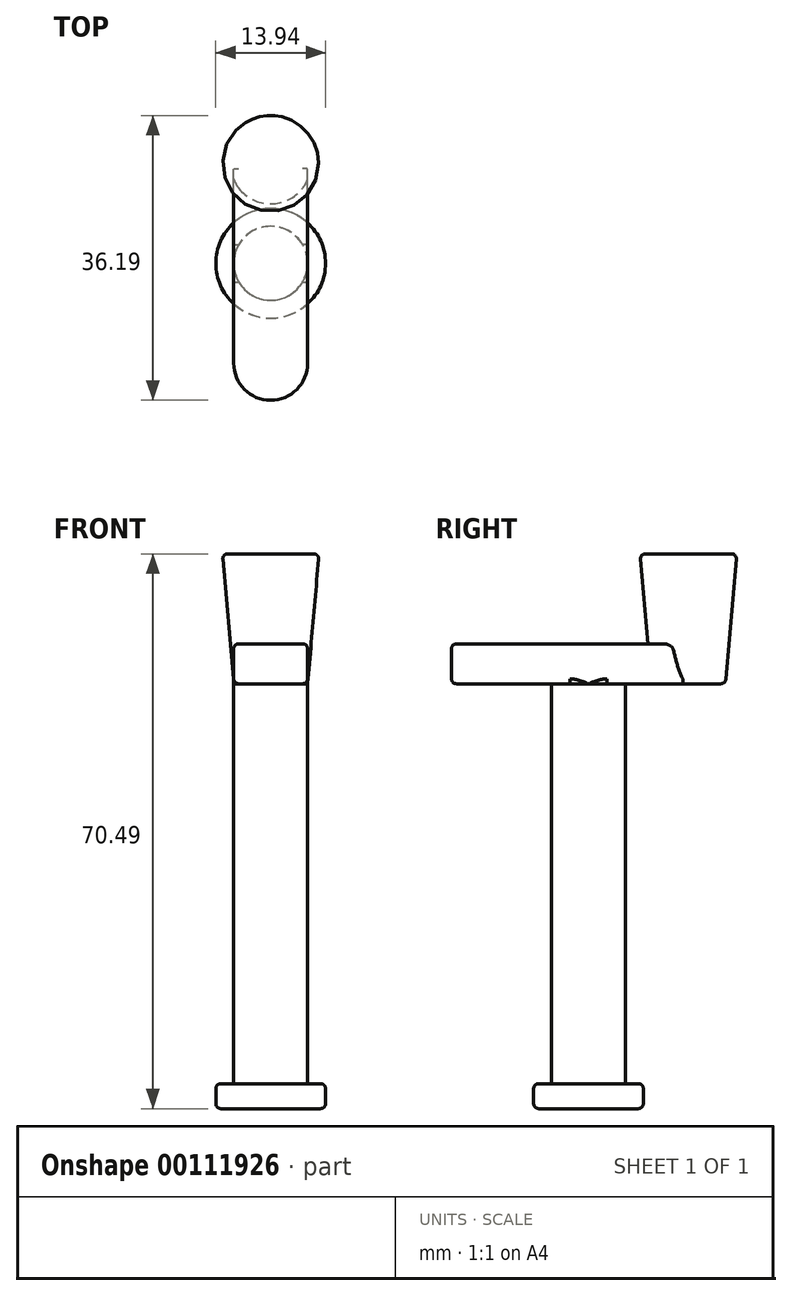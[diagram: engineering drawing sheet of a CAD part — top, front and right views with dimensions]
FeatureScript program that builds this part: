
annotation { "Feature Type Name" : "Feature", "Feature Type Description" : "" }
export const myFeature = defineFeature(function(context is Context, id is Id, definition is map)
    precondition{}
    {
        {
            var Q0;
            Q0=qCreatedBy(makeId("Top.planeOp"),FACE);
            var sketch = newSketch(context, id + "F0", { "sketchPlane" : qUnion([Q0])});
            skLineSegment(sketch, "E0.bottom", {"start": v(4.7, -12.7) * mm, "end": v(-4.7, -12.7) * mm});
            skLineSegment(sketch, "E0.top", {"start": v(4.7, 12.7) * mm, "end": v(-4.7, 12.7) * mm});
            skLineSegment(sketch, "E0.left", {"start": v(4.7, -12.7) * mm, "end": v(4.7, 12.7) * mm});
            skLineSegment(sketch, "E0.right", {"start": v(-4.7, -12.7) * mm, "end": v(-4.7, 12.7) * mm});
            skPoint(sketch, "E0.middle", {"position": v(0, 0) * mm});
            skCircle(sketch, "E1", {"center": v(0, 12.7) * mm, "radius": 4.7 * mm});
            skCircle(sketch, "E2", {"center": v(0, -12.7) * mm, "radius": 4.7 * mm});
            skSolve(sketch);
        }
        {
            var Q0;
            {var subQ0=sQuery(id+"F0.wireOp",EDGE,"E0.left");Q0=makeQuery(id+"F0.imprint","IMPRINT",FACE,{"disambiguationData":[TD([[makeQuery(id+"F0.imprint","IMPRINT",EDGE,{"derivedFrom":subQ0}),1.0]])]});}
            var Q1;
            {var subQ0=sQuery(id+"F0.wireOp",EDGE,"E0.bottom");Q1=makeQuery(id+"F0.imprint","IMPRINT",FACE,{"disambiguationData":[TD([[makeQuery(id+"F0.imprint","IMPRINT",EDGE,{"derivedFrom":subQ0}),1.0]])]});}
            var Q2;
            {var subQ0=sQuery(id+"F0.wireOp",EDGE,"E0.bottom");Q2=makeQuery(id+"F0.imprint","IMPRINT",FACE,{"disambiguationData":[TD([[makeQuery(id+"F0.imprint","IMPRINT",EDGE,{"derivedFrom":subQ0}),-1.0]])]});}
            extrude(context, id + "F1", {"entities" : qUnion([Q0, Q1, Q2]), "depth" : 5.08 * mm});
        }
        {
            var Q0;
            {var subQ0=sQuery(id+"F0.wireOp",EDGE,"E0.top");Q0=makeQuery(id+"F0.imprint","IMPRINT",FACE,{"disambiguationData":[TD([[makeQuery(id+"F0.imprint","IMPRINT",EDGE,{"derivedFrom":subQ0}),1.0]])]});}
            var Q1;
            {var subQ0=sQuery(id+"F0.wireOp",EDGE,"E0.top");Q1=makeQuery(id+"F0.imprint","IMPRINT",FACE,{"disambiguationData":[TD([[makeQuery(id+"F0.imprint","IMPRINT",EDGE,{"derivedFrom":subQ0}),-1.0]])]});}
            extrude(context, id + "F2", {"entities" : qUnion([Q0, Q1]), "operationType" : NewBodyOperationType.ADD, "depth" : 16.5 * mm, "hasDraft" : true, "draftAngle" : 5 * degree});
        }
        {
            var Q0;
            {var subQ0=sQuery(id+"F0.wireOp",EDGE,"E1");Q0=makeQuery(id+"F2.boolean.opBoolean","MERGE",FACE,{"derivedFrom":[makeQuery(id+"F1.opExtrude","CAP_FACE",FACE,{"disambiguationData":[OSD([sQuery(id+"F0.wireOp",EDGE,"E0.left"),sQuery(id+"F0.wireOp",EDGE,"E0.right"),subQ0,sQuery(id+"F0.wireOp",EDGE,"E2")])],"isStart":true}),makeQuery(id+"F2.opExtrude","CAP_FACE",FACE,{"disambiguationData":[OSD([subQ0])],"isStart":true})]});}
            var sketch = newSketch(context, id + "F3", { "sketchPlane" : qUnion([Q0])});
            skCircle(sketch, "E3", {"center": v(0, 0) * mm, "radius": 4.7 * mm});
            skSolve(sketch);
        }
        {
            var Q0;
            {var subQ0=sQuery(id+"F3.wireOp",EDGE,"E3");var subQ1=makeQuery(id+"F3.imprint","INTERSECT",VERTEX,{"derivedFrom":[makeQuery(id+"F1.opExtrude","CAP_EDGE",EDGE,{"disambiguationData":[OSD([sQuery(id+"F0.wireOp",EDGE,"E0.left")])],"isStart":true}),subQ0]});Q0=makeQuery(id+"F3.imprint","IMPRINT",FACE,{"disambiguationData":[TD([[makeQuery(id+"F3.imprint","IMPRINT",EDGE,{"disambiguationData":[TD([[subQ1,-1.0]])],"derivedFrom":subQ0}),1.0]])]});}
            extrude(context, id + "F4", {"entities" : qUnion([Q0]), "operationType" : NewBodyOperationType.ADD, "depth" : 50.8 * mm});
        }
        {
            var Q0;
            Q0=makeQuery(id+"F2.opExtrude","CAP_EDGE",EDGE,{"disambiguationData":[OSD([sQuery(id+"F0.wireOp",EDGE,"E1")])],"isStart":false});
            var Q1;
            Q1=makeQuery(id+"F1.opExtrude","CAP_EDGE",EDGE,{"disambiguationData":[OSD([sQuery(id+"F0.wireOp",EDGE,"E2")])],"isStart":false});
            var Q2;
            Q2=makeQuery(id+"F1.opExtrude","CAP_EDGE",EDGE,{"disambiguationData":[OSD([sQuery(id+"F0.wireOp",EDGE,"E2")])],"isStart":true});
            var Q3;
            {var subQ1=sQuery(id+"F0.wireOp",EDGE,"E0.right");var subQ2=sQuery(id+"F0.wireOp",EDGE,"E2");Q3=makeQuery(id+"F4.boolean.opBoolean","SPLIT",EDGE,{"disambiguationData":[TD([makeQuery(id+"F1.opExtrude","SWEPT_FACE",FACE,{"disambiguationData":[OSD([subQ2])]})])],"derivedFrom":makeQuery(id+"F1.opExtrude","CAP_EDGE",EDGE,{"disambiguationData":[OSD([subQ1])],"isStart":true})});}
            var Q4;
            {var subQ0=sQuery(id+"F0.wireOp",EDGE,"E1");var subQ1=sQuery(id+"F0.wireOp",EDGE,"E0.right");Q4=makeQuery(id+"F4.boolean.opBoolean","SPLIT",EDGE,{"disambiguationData":[TD([makeQuery(id+"F2.opExtrude","SWEPT_FACE",FACE,{"disambiguationData":[OSD([subQ0])]})])],"derivedFrom":makeQuery(id+"F1.opExtrude","CAP_EDGE",EDGE,{"disambiguationData":[OSD([subQ1])],"isStart":true})});}
            var Q5;
            Q5=makeQuery(id+"F2.opExtrude","CAP_EDGE",EDGE,{"disambiguationData":[OSD([sQuery(id+"F0.wireOp",EDGE,"E1")])],"isStart":true});
            var Q6;
            {var subQ0=sQuery(id+"F0.wireOp",EDGE,"E1");var subQ1=sQuery(id+"F0.wireOp",EDGE,"E0.left");Q6=makeQuery(id+"F4.boolean.opBoolean","SPLIT",EDGE,{"disambiguationData":[TD([makeQuery(id+"F2.opExtrude","SWEPT_FACE",FACE,{"disambiguationData":[OSD([subQ0])]})])],"derivedFrom":makeQuery(id+"F1.opExtrude","CAP_EDGE",EDGE,{"disambiguationData":[OSD([subQ1])],"isStart":true})});}
            var Q7;
            Q7=makeQuery(id+"F1.opExtrude","CAP_EDGE",EDGE,{"disambiguationData":[OSD([sQuery(id+"F0.wireOp",EDGE,"E0.left")])],"isStart":false});
            fillet(context, id + "F5", {"entities" : qUnion([Q0, Q1, Q2, Q3, Q4, Q5, Q6, Q7]), "radius" : 0.64 * mm, "tangentPropagation" : true, "allowEdgeOverflow" : false});
        }
        {
            var Q0;
            Q0=makeQuery(id+"F4.opExtrude","CAP_FACE",FACE,{"disambiguationData":[OSD([sQuery(id+"F3.wireOp",EDGE,"E3")])],"isStart":false});
            var sketch = newSketch(context, id + "F6", { "sketchPlane" : qUnion([Q0])});
            skCircle(sketch, "E4", {"center": v(0, 0) * mm, "radius": 6.97 * mm});
            skSolve(sketch);
        }
        {
            var Q0;
            Q0 = qSketchRegion(id + "F6", true);
            extrude(context, id + "F7", {"entities" : qUnion([Q0]), "operationType" : NewBodyOperationType.ADD, "depth" : 3.17 * mm});
        }
        {
            var Q0;
            Q0=makeQuery(id+"F4.opExtrude","CAP_EDGE",EDGE,{"disambiguationData":[OSD([sQuery(id+"F3.wireOp",EDGE,"E3")])],"isStart":false});
            var Q1;
            Q1=makeQuery(id+"F7.opExtrude","CAP_EDGE",EDGE,{"disambiguationData":[OSD([sQuery(id+"F6.wireOp",EDGE,"E4")])],"isStart":true});
            var Q2;
            Q2=makeQuery(id+"F7.opExtrude","CAP_EDGE",EDGE,{"disambiguationData":[OSD([sQuery(id+"F6.wireOp",EDGE,"E4")])],"isStart":false});
            fillet(context, id + "F8", {"entities" : qUnion([Q0, Q1, Q2]), "radius" : 0.64 * mm, "tangentPropagation" : true, "allowEdgeOverflow" : false});
        }
    });
